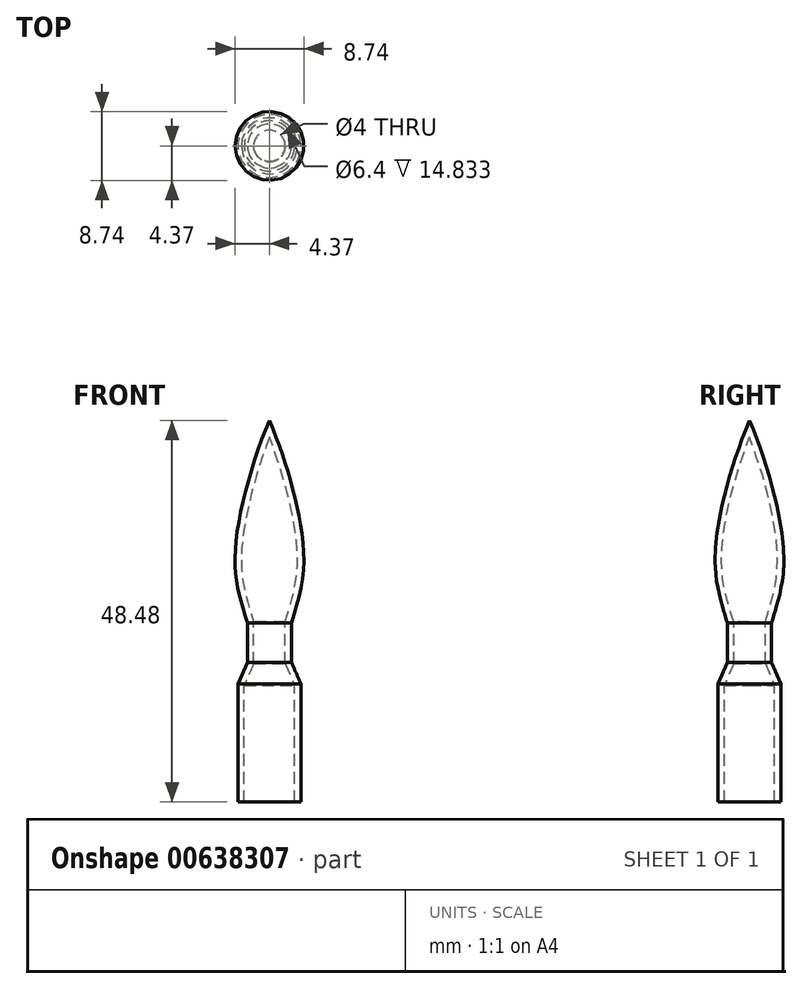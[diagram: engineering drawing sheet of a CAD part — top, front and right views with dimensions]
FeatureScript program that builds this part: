
annotation { "Feature Type Name" : "Feature", "Feature Type Description" : "" }
export const myFeature = defineFeature(function(context is Context, id is Id, definition is map)
    precondition{}
    {
        {
            var Q0;
            Q0=qCreatedBy(makeId("Front.planeOp"),FACE);
            var sketch = newSketch(context, id + "F0", { "sketchPlane" : qUnion([Q0])});
            skFitSpline(sketch, "E0", {"points": [v(0, 31.27) * mm, v(-4.35, 14.47) * mm, v(-2.8, 5.54) * mm], "startDerivative": vector(-11.42, -26.76) * mm, "endDerivative": vector(7, -22.8) * mm});
            skLineSegment(sketch, "E1", {"start": v(-2.8, 5.54) * mm, "end": v(-2.8, 0.54) * mm});
            skLineSegment(sketch, "E2", {"start": v(-2.8, 0.54) * mm, "end": v(-4, -2.2) * mm});
            skLineSegment(sketch, "E3", {"start": v(-4, -2.2) * mm, "end": v(-4, -17.2) * mm});
            skLineSegment(sketch, "E4", {"start": v(-4, -17.2) * mm, "end": v(0, -17.2) * mm});
            skLineSegment(sketch, "E5", {"start": v(0, 31.27) * mm, "end": v(0, -17.2) * mm});
            skLineSegment(sketch, "E6", {"start": v(-2.8, 0.54) * mm, "end": v(0, 0.54) * mm});
            skSolve(sketch);
        }
        {
            var Q0;
            Q0 = qSketchRegion(id + "F0", true);
            var Q1;
            Q1=sQuery(id+"F0.wireOp",EDGE,"E5");
            revolve(context, id + "F1", {"entities" : qUnion([Q0]), "axis" : qUnion([Q1]), "revolveType" : RevolveType.FULL});
        }
        {
            var Q0;
            Q0=makeQuery(id+"F1.opRevolve","SWEPT_FACE",FACE,{"disambiguationData":[OSD([sQuery(id+"F0.wireOp",EDGE,"E4")])]});
            shell(context, id + "F2", {"entities" : qUnion([Q0]), "thickness" : 0.8 * mm});
        }
    });
